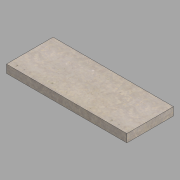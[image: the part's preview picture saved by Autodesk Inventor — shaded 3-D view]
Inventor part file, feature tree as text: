
AUTODESK INVENTOR PART (.ipt)
format: ipt  version: 2022.2 (Build 262287000, 287)  size: 108,032 bytes
history: native  units: in
note: dims shown in document units (in); Inventor stores cm internally (conversion verified against a paired STEP export)
features: extrude x1, sketch x1
ambient origin geometry x8: Origin, YZ Plane, XZ Plane, XY Plane, X Axis, Y Axis, Z Axis, Center Point
bodies: Solid1 (feature_tree)
feature tree (2):
  extrude  "Extrusion1"  Depth=23.0in
  sketch  "Sketch1"  dims[d0=4.0in d1=23.0in d2=59.375in d3=0.0in]
